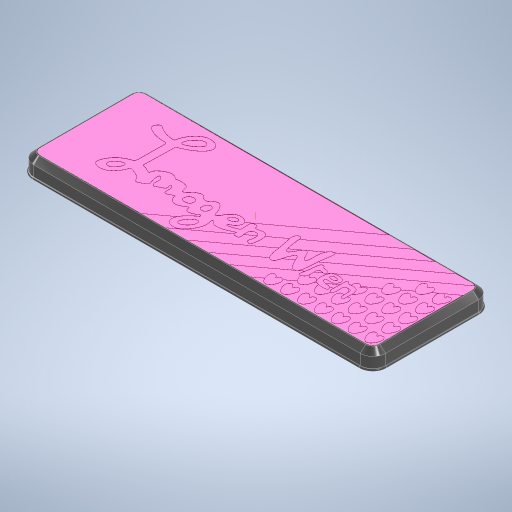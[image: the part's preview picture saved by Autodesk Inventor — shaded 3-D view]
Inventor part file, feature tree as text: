
AUTODESK INVENTOR PART (.ipt)
format: ipt  version: 2024.1 (Build 281209000, 209)  size: 2,149,376 bytes
history: native  units: mm
features: projected_geometry x29, extrude x20, fillet x11, chamfer x5, other x4, pattern_circular x2, sketch x2, plane x1, pattern_linear x1, mirror x1
ambient origin geometry x8: Origin, YZ Plane, XZ Plane, XY Plane, X Axis, Y Axis, Z Axis, Center Point
bodies: Body1 (feature_tree), Body2 (feature_tree), Body3 (feature_tree)
feature tree (76):
  other  "case"
  extrude  "Extrusion1"  Depth=56.0mm
  extrude  "Extrusion2"  Depth=28.0mm
  extrude  "Extrusion3"  Depth=18.0mm TaperAngle=0.0deg
  fillet  "Fillet1"  Radius=2.0mm
  fillet  "Fillet2"  Radius=4.0mm
  fillet  "Fillet3"  Radius=20.0mm
  pattern_circular  "Circular Pattern1"  [2 undecoded]
  fillet  "Fillet4"  Radius=20.0mm
  chamfer  "Chamfer1"  Distance=96.0mm
  extrude  "Extrusion4"  Depth=65.0mm
  chamfer  "Chamfer2"  Distance=74.2mm
  extrude  "Extrusion5"  Depth=12.0mm
  pattern_circular  "Circular Pattern2"  [2 undecoded]
  fillet  "Fillet5"  Radius=12.4mm
  fillet  "Fillet6"  Radius=0.95mm
  fillet  "Fillet10"  Radius=0.95mm
  fillet  "Fillet11"  Radius=2.0mm
  fillet  "Fillet12"  Radius=3.7mm
  extrude  "Extrusion6"  Depth=17.6mm TaperAngle=0.0deg
  plane  "Work Plane1"
  extrude  "Extrusion7"  Depth=25.0mm
  extrude  "Extrusion8"  Depth=16.6mm
  extrude  "Extrusion9"  Depth=4.0mm
  fillet  "Fillet8"  Radius=3.0mm
  extrude  "Extrusion10"  Depth=4.0mm
  pattern_linear  "Rectangular Pattern1"  Count1=2 Spacing1=180.0deg
  mirror  "Mirror1"
  extrude  "Extrusion11"  Depth=6.0mm
  extrude  "Extrusion15"  Depth=6.0mm TaperAngle=45.0deg
  extrude  "Extrusion16"  Depth=1.3mm
  chamfer  "Chamfer4"  Distance=5.0mm
  extrude  "Extrusion18"  Depth=3.0mm TaperAngle=45.0deg
  extrude  "Extrusion19"  Depth=6.0mm
  extrude  "Extrusion12"  Depth=6.5mm
  extrude  "Extrusion13"  Depth=6.5mm
  extrude  "Extrusion14"  Depth=22.0mm
  extrude  "Extrusion17"  Depth=2.0mm TaperAngle=0.0deg
  chamfer  "Chamfer5"  Distance=20.0mm Angle=360.0deg
  chamfer  "Chamfer6"  Distance=6.5mm
  extrude  "Extrusion20"  Depth=6.5mm
  fillet  "Fillet13"  Radius=2.0mm
  projected_geometry  "Projected Loop1"
  projected_geometry  "Projected Loop5"
  other  "Work Axis1"
  projected_geometry  "Projected Loop7"
  other  "lid"
  projected_geometry  "Projected Loop8"
  projected_geometry  "Projected Loop9"
  projected_geometry  "Projected Loop10"
  projected_geometry  "Projected Loop11"
  sketch  "Sketch15"  dims[d0=167.0mm d1=56.0mm]
  sketch  "Sketch16"  dims[d2=83.5mm d3=28.0mm d4=18.0mm d5=0.0mm d6=2.0mm d8=4.0mm d9=20.0mm d10=4.0mm d11=20.0mm d12=96.0mm d13=65.0mm d14=74.2mm d15=12.0mm d16=14.3mm d17=12.4mm d18=0.95mm d19=0.95mm d20=2.0mm d21=3.7mm d22=17.6mm d23=0.0mm d24=25.0mm d27=16.6mm d28=-1.745329mm d29=4.0mm d30=3.0mm d31=4.0mm d32=20.0mm d33=180.0deg d35=6.0mm d36=6.0mm d37=2.0mm d38=45.0deg d39=1.3mm d40=5.0mm d41=0.0mm d42=3.0mm d43=2.0mm d44=45.0deg d45=6.0mm d46=6.5mm d47=6.5mm d48=22.0mm d49=2.0mm d50=0.0mm d51=20.0mm d52=360.0deg d54=6.5mm d55=6.5mm d56=2.0mm d57=3.0mm d59=6.5mm d60=6.45mm d61=1.0mm d62=3.0mm d63=0.0mm d64=3.1mm d65=0.0mm d69=1.8mm d70=0.0mm d71=0.5mm d72=1.0mm d73=0.0mm d74=0.5mm d75=60.0mm d76=20.0mm d77=29.0mm d79=8.5mm d80=-1.745329mm d82=70.0mm d84=124.0mm d85=55.0mm d86=1.0mm d89=0.06mm d90=0.0mm d91=0.02mm d92=0.0mm d93=30.0deg d94=1.0mm d95=6.0mm d96=6.0mm d97=7.0mm d98=6.0mm d99=6.0mm d101=1.0mm d108=3.0mm d109=3.0mm d110=0.04mm d111=0.0mm d112=1.6mm d113=1.6mm d114=1.1mm d115=1.1mm d116=7.0mm d117=3.0mm d119=2.0mm d120=1.1mm d121=1.1mm d122=1.5mm d123=1.5mm d124=1.5mm d125=1.0mm d126=1.1mm d127=1.1mm d128=1.8mm d131=2.0mm d132=1.5mm d133=1.5mm d140=50.0mm d142=8.0mm d143=60.0mm d145=8.0mm d148=0.0mm d149=0.0mm d150=0.0mm d151=0.0mm d152=3.5mm d153=0.0mm d154=2.5mm d155=2.0mm d156=45.0deg d158=0.4mm d159=0.4mm d160=0.0mm d163=3.0mm d164=1.5mm d165=0.4mm d166=0.0mm d167=3.1mm d168=0.0mm d169=1.5mm d170=2.0mm d171=45.0deg d172=1.5mm d173=2.0mm d174=45.0deg d175=8.0mm d176=8.0mm d177=45.0mm d178=16.0mm d179=3.0mm d180=3.0mm d181=3.0mm d182=0.0mm d183=0.0mm d184=1.0mm]
  other  "lid-part2"
  projected_geometry  "Projected Loop12"
  projected_geometry  "Projected Loop13"
  projected_geometry  "Projected Loop14"
  projected_geometry  "Projected Loop15"
  projected_geometry  "Projected Loop16"
  projected_geometry  "Projected Loop17"
  projected_geometry  "Projected Loop18"
  projected_geometry  "Projected Loop19"
  projected_geometry  "Projected Loop20"
  projected_geometry  "Projected Loop21"
  projected_geometry  "Projected Loop22"
  projected_geometry  "Projected Loop23"
  projected_geometry  "Projected Loop24"
  projected_geometry  "Projected Loop25"
  projected_geometry  "Projected Loop26"
  projected_geometry  "Projected Loop27"
  projected_geometry  "Projected Loop28"
  projected_geometry  "Projected Loop29"
  projected_geometry  "Projected Loop30"
  projected_geometry  "Projected Loop31"
  projected_geometry  "Projected Loop32"
  projected_geometry  "Projected Loop33"
note: 4 required parameter values undecoded (feature->parameter linkage not recoverable at this tier; creation-order binding heuristic only, values carry confidence <= 0.55)
